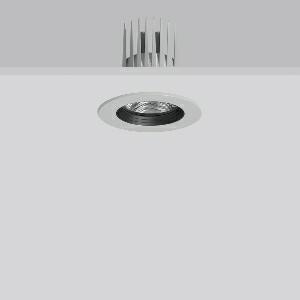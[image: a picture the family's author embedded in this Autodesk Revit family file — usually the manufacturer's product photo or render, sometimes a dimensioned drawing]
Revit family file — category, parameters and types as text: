
# Revit family: heledon_mini_e_901750_004_3_ec65
name_source: partatom
category: Lighting Fixtures
units: mm (PartAtom-declared; Revit-internal decimal feet)

## family parameters
Cut with Voids When Loaded = No
Host = Face
Light Source = No
Part Type = Normal
Room Calculation Point = No
Round Connector Dimension = Use Diameter
Shared = No

## types (1)
- HELEDON mini E (1 x LED Modul 935, 3800 lm, 3500)
    Apparent Load = 29 VA
    Approval mark = CE
    CIE Flux Codes = 95 99 100 100 100
    Color Rendering = 92
    Color Temperature = 3500
    Default Elevation = 1800 mm
    Description = Series: HELEDON mini
Round recessed downlight. Housing: die-cast aluminium, powder-coated. Black plastic ring and recessed LED to prevent glare from the side. Optical assembly with reflector made of MIRO-Silver with 98% total light reflection for outstanding efficiency - can be changed without tools. Best colour rendering index Ra>90. Suitable for Recessed ceiling mounting. Installation without tools thanks to spring fastening system. Including separate LED converter with connecting cable 600 mm.High quality converter without flickering and stroboscopic effect. Through-wiring box (5 pole) available as accessory. The following accessories can be mounted without use of tools: interchangeable lenses, decorative glasses, honeycomb louvre, clear and frosted diffusers, white interchangeable plastic ring. 
Colour: silver
Diameter: 124 mm
Height: 3 mm
Cut-out diameter: 114 mm
Recess height: 170 mm
Luminaire: recess height: 120 mm
Lamp: LED
Socket: without socket
Colour temperature: 3500K
Colour rendering index (CRI): 92
System power: 29 W
Rated luminous flux: 3800 lm
Luminous efficiency: 131 lm/W
Control gear: Regulated power supply
Protection class: II
Type of protection: IP 20
    Height = 0 mm  [stored 0 ft]
    Lamp = 1 x LED Modul 935
    Lamp Light Flux = 3800 lm
    Lamp count = 1
    Length = 124 mm  [stored 0.406824 ft]
    Lifetime = 50000 h
    Luminous efficacy = 131 lm/W
    Manufacturer = RZB
    ModVariant = No
    Model = 901750.004.3
    Mounting Place = Ceiling
    Mounting Type = Recessed
    Number of Poles = 1
    OnlyDefault = Yes
    Power Factor = 1
    Product Name = HELEDON mini E
    Product group = Recessed downlights
    ProductGroupID = 402
    Protection Class = Protection class II
    Protection Degree = IP 20
    RLX_Detail_Level = 1
    RLX_Emergency_Light_Flux = 0 lm
    RLX_Emergency_Type = 0
    RLX_Emergency_Type_DB = No
    RlxData = <blob elided: 125665 chars, md5=33fc7d21>
    Socket = socket
    Standby Power = 0 W
    System Light Flux = 3800 lm
    System Power = 29 W
    Type Comments = Product without accessories
    Type Image = 901657.004.jpg
    URL = http://relux.com
    VarID = ---
    Voltage = 230 V
    Voltage Range = 220-240 V
    Weight = 0.00 kg
    Width = 0 mm  [stored 0 ft]

note: [stored X ft] marks values corroborated as IEEE doubles in the binary element streams (Revit-internal decimal feet)

## geometry (parser evidence)
native form markers: Blend x4, Sweep x11
no freeform markers — native parametric forms only
